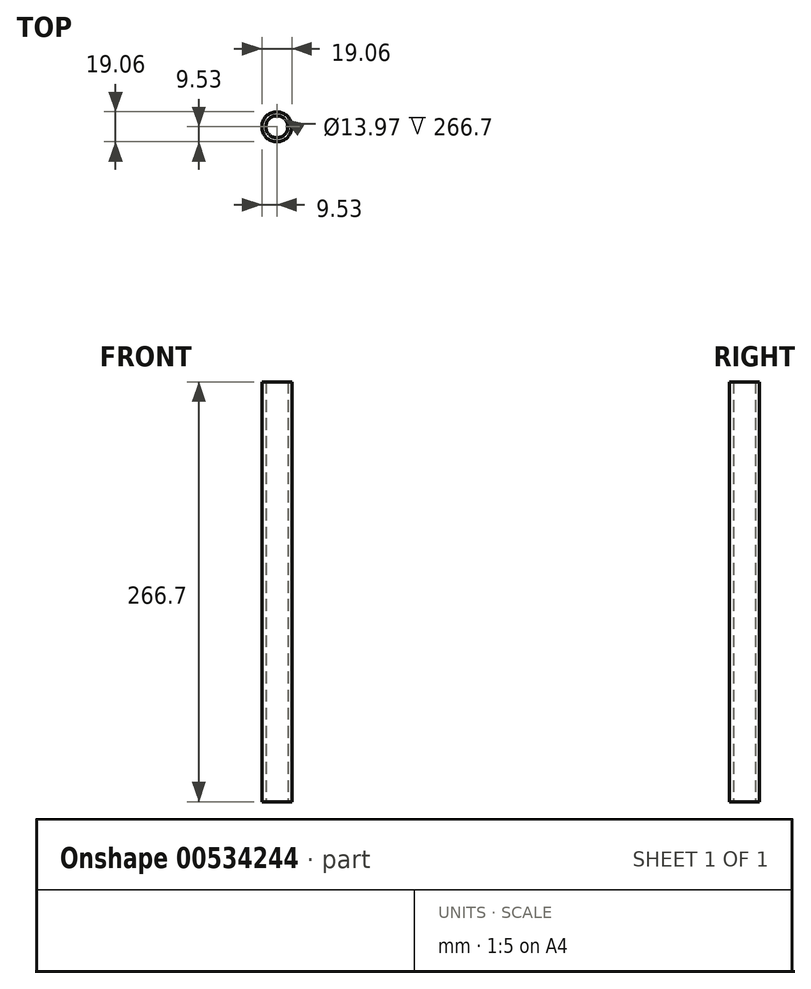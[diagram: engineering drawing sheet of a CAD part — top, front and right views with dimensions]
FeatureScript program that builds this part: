
annotation { "Feature Type Name" : "Feature", "Feature Type Description" : "" }
export const myFeature = defineFeature(function(context is Context, id is Id, definition is map)
    precondition{}
    {
        {
            var Q0;
            Q0=qCreatedBy(makeId("Top.planeOp"),FACE);
            var sketch = newSketch(context, id + "F0", { "sketchPlane" : qUnion([Q0])});
            skCircle(sketch, "E0", {"center": v(0, 0) * mm, "radius": 9.53 * mm});
            skLineSegment(sketch, "E1", {"start": v(0, 9.53) * mm, "end": v(0, -9.53) * mm});
            skSolve(sketch);
        }
        {
            var Q0;
            {var subQ0=sQuery(id+"F0.wireOp",EDGE,"E1");Q0=makeQuery(id+"F0.imprint","IMPRINT",FACE,{"disambiguationData":[TD([[makeQuery(id+"F0.imprint","IMPRINT",EDGE,{"derivedFrom":subQ0}),-1.0]])]});}
            var Q1;
            {var subQ0=sQuery(id+"F0.wireOp",EDGE,"E1");Q1=makeQuery(id+"F0.imprint","IMPRINT",FACE,{"disambiguationData":[TD([[makeQuery(id+"F0.imprint","IMPRINT",EDGE,{"derivedFrom":subQ0}),1.0]])]});}
            extrude(context, id + "F1", {"entities" : qUnion([Q0, Q1]), "depth" : 266.7 * mm, "offsetDistance" : 25.4 * mm});
        }
        {
            var Q0;
            Q0=makeQuery(id+"F1.opExtrude","CAP_FACE",FACE,{"disambiguationData":[OSD([sQuery(id+"F0.wireOp",EDGE,"E0")])],"isStart":false});
            var Q1;
            Q1=makeQuery(id+"F1.opExtrude","CAP_FACE",FACE,{"disambiguationData":[OSD([sQuery(id+"F0.wireOp",EDGE,"E0")])],"isStart":true});
            shell(context, id + "F2", {"entities" : qUnion([Q0, Q1]), "thickness" : 2.54 * mm});
        }
    });
